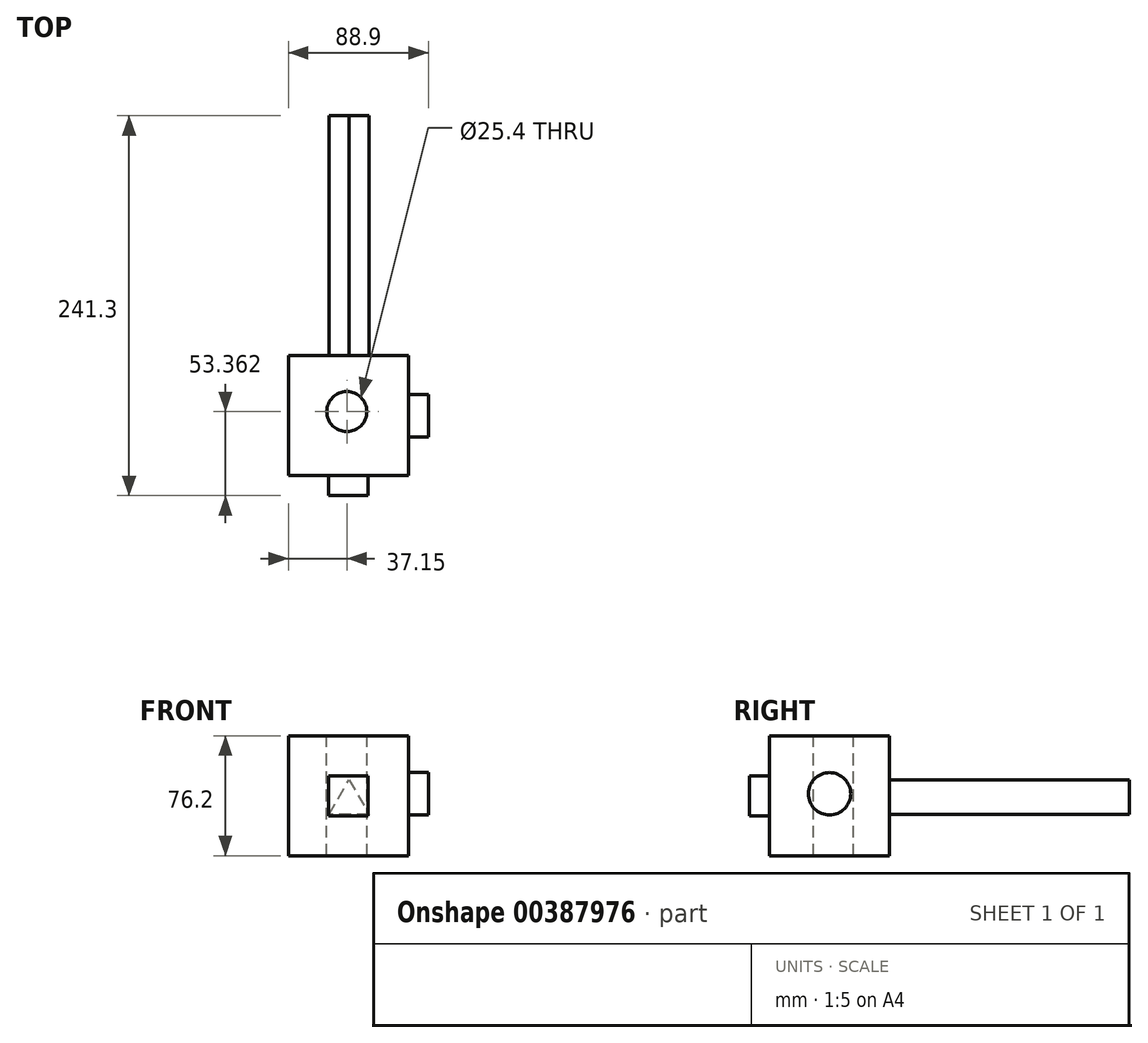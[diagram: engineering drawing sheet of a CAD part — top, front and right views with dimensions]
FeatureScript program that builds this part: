
annotation { "Feature Type Name" : "Feature", "Feature Type Description" : "" }
export const myFeature = defineFeature(function(context is Context, id is Id, definition is map)
    precondition{}
    {
        {
            var Q0;
            Q0=qCreatedBy(makeId("Front.planeOp"),FACE);
            var sketch = newSketch(context, id + "F0", { "sketchPlane" : qUnion([Q0])});
            skLineSegment(sketch, "E0.bottom", {"start": v(-37.15, 49.93) * mm, "end": v(39.05, 49.93) * mm});
            skLineSegment(sketch, "E0.top", {"start": v(-37.15, -26.27) * mm, "end": v(39.05, -26.27) * mm});
            skLineSegment(sketch, "E0.left", {"start": v(-37.15, 49.93) * mm, "end": v(-37.15, -26.27) * mm});
            skLineSegment(sketch, "E0.right", {"start": v(39.05, 49.93) * mm, "end": v(39.05, -26.27) * mm});
            skSolve(sketch);
        }
        {
            var Q0;
            Q0=makeQuery(id+"F0.imprint","IMPRINT",FACE,{"disambiguationData":[TD([[makeQuery(id+"F0.imprint","IMPRINT",EDGE,{"derivedFrom":sQuery(id+"F0.wireOp",EDGE,"E0.bottom")}),-1.0]])]});
            extrude(context, id + "F1", {"entities" : qUnion([Q0]), "depth" : 76.2 * mm});
        }
        {
            var Q0;
            Q0=makeQuery(id+"F1.opExtrude","SWEPT_FACE",FACE,{"disambiguationData":[OSD([sQuery(id+"F0.wireOp",EDGE,"E0.bottom")])]});
            var sketch = newSketch(context, id + "F2", { "sketchPlane" : qUnion([Q0])});
            skPoint(sketch, "E1", {"position": v(0, -35.54) * mm});
            skSolve(sketch);
        }
        {
            var Q0;
            Q0=sQuery(id+"F2.wireOp",VERTEX,"E1");
            var Q1;
            Q1=makeQuery(id+"F1.opExtrude","SWEPT_BODY",BODY,{"disambiguationData":[OSD([sQuery(id+"F0.wireOp",EDGE,"E0.bottom"),sQuery(id+"F0.wireOp",EDGE,"E0.top"),sQuery(id+"F0.wireOp",EDGE,"E0.left"),sQuery(id+"F0.wireOp",EDGE,"E0.right")])]});
            hole(context, id + "F3", {"style" : HoleStyle.SIMPLE, "endStyle" : HoleEndStyle.THROUGH, "holeDiameter" : 25.4 * mm, "isTappedThrough" : true, "tappedDepth" : 12.7 * mm, "tapClearance" : 3, "locations" : qUnion([Q0]), "scope" : qUnion([Q1])});
        }
        {
            var Q0;
            Q0=makeQuery(id+"F1.opExtrude","CAP_FACE",FACE,{"disambiguationData":[OSD([sQuery(id+"F0.wireOp",EDGE,"E0.bottom"),sQuery(id+"F0.wireOp",EDGE,"E0.top"),sQuery(id+"F0.wireOp",EDGE,"E0.left"),sQuery(id+"F0.wireOp",EDGE,"E0.right")])],"isStart":false});
            var sketch = newSketch(context, id + "F4", { "sketchPlane" : qUnion([Q0])});
            skLineSegment(sketch, "E2.bottom", {"start": v(-11.75, 24.53) * mm, "end": v(13.65, 24.53) * mm});
            skLineSegment(sketch, "E2.top", {"start": v(-11.75, -0.87) * mm, "end": v(13.65, -0.87) * mm});
            skLineSegment(sketch, "E2.left", {"start": v(-11.75, 24.53) * mm, "end": v(-11.75, -0.87) * mm});
            skLineSegment(sketch, "E2.right", {"start": v(13.65, 24.53) * mm, "end": v(13.65, -0.87) * mm});
            skSolve(sketch);
        }
        {
            var Q0;
            Q0=makeQuery(id+"F4.imprint","IMPRINT",FACE,{"disambiguationData":[TD([[makeQuery(id+"F4.imprint","IMPRINT",EDGE,{"derivedFrom":sQuery(id+"F4.wireOp",EDGE,"E2.bottom")}),-1.0]])]});
            extrude(context, id + "F5", {"entities" : qUnion([Q0]), "operationType" : NewBodyOperationType.ADD, "depth" : 12.7 * mm});
        }
        {
            var Q0;
            Q0=makeQuery(id+"F1.opExtrude","SWEPT_FACE",FACE,{"disambiguationData":[OSD([sQuery(id+"F0.wireOp",EDGE,"E0.right")])]});
            var sketch = newSketch(context, id + "F6", { "sketchPlane" : qUnion([Q0])});
            skCircle(sketch, "E3", {"center": v(-38.1, 13.06) * mm, "radius": 13.45 * mm});
            skSolve(sketch);
        }
        {
            var Q0;
            Q0=makeQuery(id+"F6.imprint","IMPRINT",FACE,{"disambiguationData":[TD([[makeQuery(id+"F6.imprint","IMPRINT",EDGE,{"derivedFrom":sQuery(id+"F6.wireOp",EDGE,"E3")}),1.0]])]});
            extrude(context, id + "F7", {"entities" : qUnion([Q0]), "operationType" : NewBodyOperationType.ADD, "depth" : 12.7 * mm});
        }
        {
            var Q0;
            Q0=makeQuery(id+"F1.opExtrude","CAP_FACE",FACE,{"disambiguationData":[OSD([sQuery(id+"F0.wireOp",EDGE,"E0.bottom"),sQuery(id+"F0.wireOp",EDGE,"E0.top"),sQuery(id+"F0.wireOp",EDGE,"E0.left"),sQuery(id+"F0.wireOp",EDGE,"E0.right")])],"isStart":true});
            var sketch = newSketch(context, id + "F8", { "sketchPlane" : qUnion([Q0])});
            skLineSegment(sketch, "E4", {"start": v(-1.44, 22) * mm, "end": v(-14.14, 0) * mm});
            skLineSegment(sketch, "E5", {"start": v(-14.14, 0) * mm, "end": v(11.26, 0) * mm});
            skLineSegment(sketch, "E6", {"start": v(11.26, 0) * mm, "end": v(-1.44, 22) * mm});
            skSolve(sketch);
        }
        {
            var Q0;
            Q0=makeQuery(id+"F8.imprint","IMPRINT",FACE,{"disambiguationData":[TD([[makeQuery(id+"F8.imprint","IMPRINT",EDGE,{"derivedFrom":sQuery(id+"F8.wireOp",EDGE,"E4")}),1.0]])]});
            extrude(context, id + "F9", {"entities" : qUnion([Q0]), "operationType" : NewBodyOperationType.ADD, "depth" : 152.4 * mm});
        }
    });
